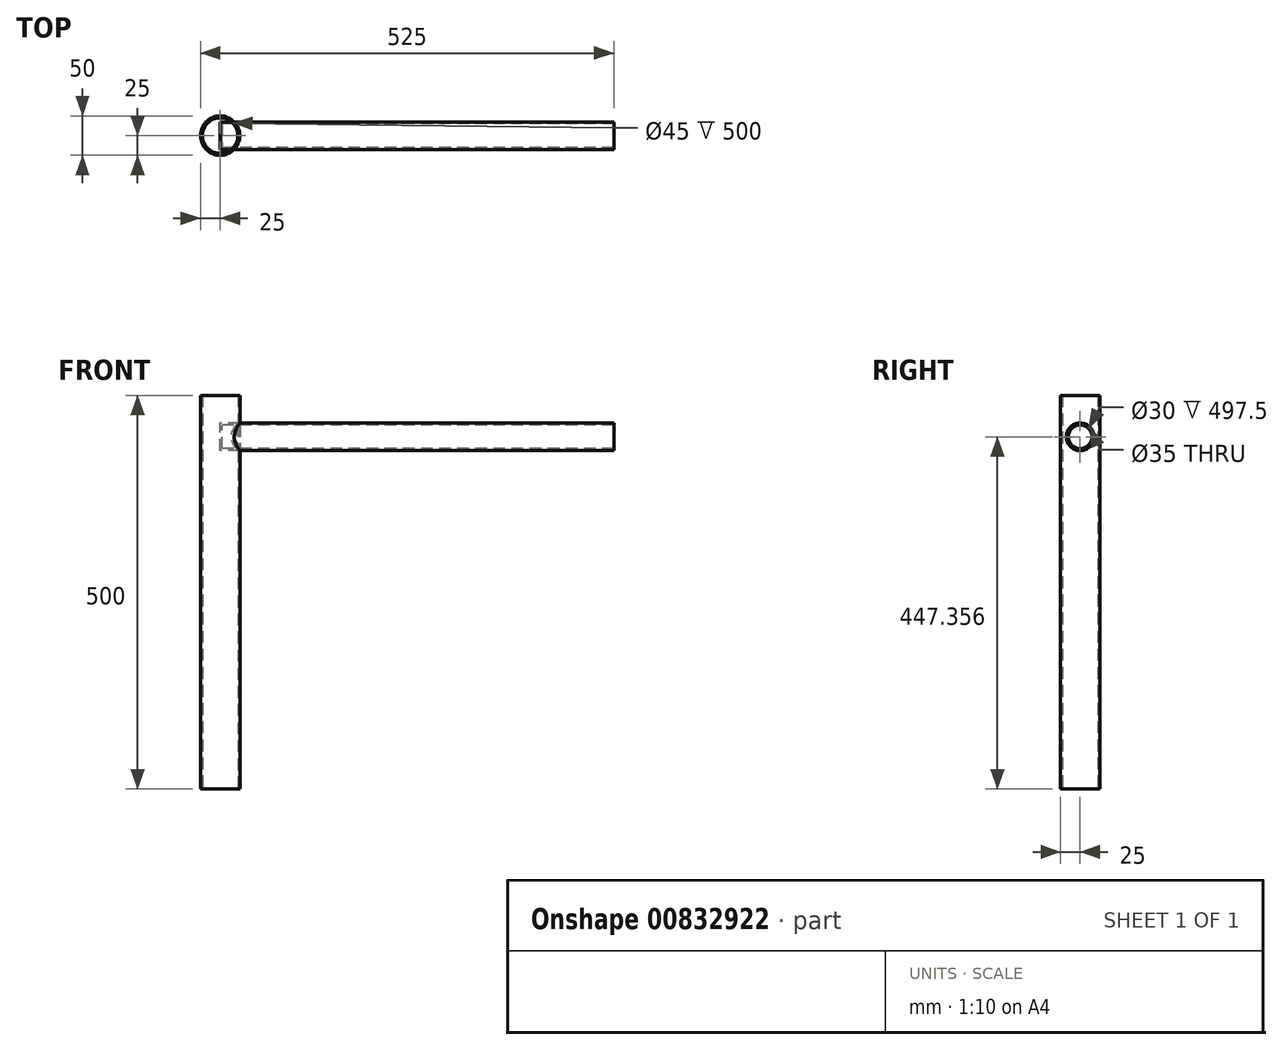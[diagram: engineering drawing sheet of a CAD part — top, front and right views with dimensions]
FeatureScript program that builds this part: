
annotation { "Feature Type Name" : "Feature", "Feature Type Description" : "" }
export const myFeature = defineFeature(function(context is Context, id is Id, definition is map)
    precondition{}
    {
        {
            var Q0;
            Q0=qCreatedBy(makeId("Top.planeOp"),FACE);
            var sketch = newSketch(context, id + "F0", { "sketchPlane" : qUnion([Q0])});
            skCircle(sketch, "E0", {"center": v(0, 0) * mm, "radius": 25 * mm});
            skSolve(sketch);
        }
        {
            var Q0;
            Q0=makeQuery(id+"F0.imprint","IMPRINT",FACE,{"disambiguationData":[TD([[makeQuery(id+"F0.imprint","IMPRINT",EDGE,{"derivedFrom":sQuery(id+"F0.wireOp",EDGE,"E0")}),1.0]])]});
            extrude(context, id + "F1", {"entities" : qUnion([Q0]), "depth" : 500 * mm, "offsetDistance" : 25 * mm});
        }
        {
            var Q0;
            Q0=qCreatedBy(makeId("Right.planeOp"),FACE);
            var sketch = newSketch(context, id + "F2", { "sketchPlane" : qUnion([Q0])});
            skCircle(sketch, "E1", {"center": v(0, 447.36) * mm, "radius": 17.5 * mm});
            skSolve(sketch);
        }
        {
            var Q0;
            Q0 = qSketchRegion(id + "F2", true);
            extrude(context, id + "F3", {"entities" : qUnion([Q0]), "depth" : 500 * mm, "offsetDistance" : 25 * mm});
        }
        {
            var Q0;
            Q0=qCreatedBy(makeId("Top.planeOp"),FACE);
            var sketch = newSketch(context, id + "F4", { "sketchPlane" : qUnion([Q0])});
            skLineSegment(sketch, "E2", {"start": v(0, 62.38) * mm, "end": v(0, -121.01) * mm});
            skSolve(sketch);
        }
        {
            var Q0;
            Q0=qCreatedBy(makeId("Top.planeOp"),FACE);
            var Q1;
            Q1=sQuery(id+"F4.wireOp",EDGE,"E2");
            cPlane(context, id + "F5", {"entities" : qUnion([Q0, Q1]), "cplaneType" : CPlaneType.LINE_ANGLE, "offset" : 25 * mm, "angle" : 45 * degree, "oppositeDirection" : true, "width" : 150 * mm, "height" : 150 * mm});
        }
        {
            var Q0;
            Q0=qCreatedBy(id+"F5.planeOp",FACE);
            var sketch = newSketch(context, id + "F6", { "sketchPlane" : qUnion([Q0])});
            skLineSegment(sketch, "E3.bottom", {"start": v(-23.2, -14.3) * mm, "end": v(7.82, -14.3) * mm});
            skLineSegment(sketch, "E3.top", {"start": v(-23.2, 14.12) * mm, "end": v(7.82, 14.12) * mm});
            skLineSegment(sketch, "E3.left", {"start": v(-23.2, -14.3) * mm, "end": v(-23.2, 14.12) * mm});
            skLineSegment(sketch, "E3.right", {"start": v(7.82, -14.3) * mm, "end": v(7.82, 14.12) * mm});
            skSolve(sketch);
        }
        {
            var Q0;
            Q0 = qSketchRegion(id + "F6", true);
            extrude(context, id + "F7", {"entities" : qUnion([Q0]), "oppositeDirection" : true, "depth" : 700 * mm, "offsetDistance" : 25 * mm});
        }
        {
            var Q0;
            Q0=makeQuery(id+"F1.opExtrude","CAP_FACE",FACE,{"disambiguationData":[OSD([sQuery(id+"F0.wireOp",EDGE,"E0")])],"isStart":true});
            var Q1;
            Q1=makeQuery(id+"F7.opExtrude","CAP_FACE",FACE,{"disambiguationData":[OSD([sQuery(id+"F6.wireOp",EDGE,"E3.bottom"),sQuery(id+"F6.wireOp",EDGE,"E3.top"),sQuery(id+"F6.wireOp",EDGE,"E3.left"),sQuery(id+"F6.wireOp",EDGE,"E3.right")])],"isStart":true});
            var Q2;
            Q2=makeQuery(id+"F3.opExtrude","CAP_FACE",FACE,{"disambiguationData":[OSD([sQuery(id+"F2.wireOp",EDGE,"E1")])],"isStart":false});
            var Q3;
            Q3=makeQuery(id+"F7.opExtrude","CAP_FACE",FACE,{"disambiguationData":[OSD([sQuery(id+"F6.wireOp",EDGE,"E3.bottom"),sQuery(id+"F6.wireOp",EDGE,"E3.top"),sQuery(id+"F6.wireOp",EDGE,"E3.left"),sQuery(id+"F6.wireOp",EDGE,"E3.right")])],"isStart":false});
            var Q4;
            Q4=makeQuery(id+"F1.opExtrude","CAP_FACE",FACE,{"disambiguationData":[OSD([sQuery(id+"F0.wireOp",EDGE,"E0")])],"isStart":false});
            shell(context, id + "F8", {"entities" : qUnion([Q0, Q1, Q2, Q3, Q4]), "thickness" : 2.5 * mm});
        }
        {
            var Q0;
            Q0=makeQuery(id+"F3.opExtrude","SWEPT_BODY",BODY,{"disambiguationData":[OSD([sQuery(id+"F2.wireOp",EDGE,"E1")])]});
            var Q1;
            Q1=makeQuery(id+"F7.opExtrude","SWEPT_BODY",BODY,{"disambiguationData":[OSD([sQuery(id+"F6.wireOp",EDGE,"E3.bottom"),sQuery(id+"F6.wireOp",EDGE,"E3.top"),sQuery(id+"F6.wireOp",EDGE,"E3.left"),sQuery(id+"F6.wireOp",EDGE,"E3.right")])]});
            booleanBodies(context, id + "F9", {"operationType" : BooleanOperationType.SUBTRACTION, "tools" : qUnion([Q0]), "targets" : qUnion([Q1]), "keepTools" : true});
        }
        {
            var Q0;
            Q0=makeQuery(id+"F9.opBoolean","SPLIT",BODY,{"disambiguationData":[OD(2.0)],"derivedFrom":makeQuery(id+"F7.opExtrude","SWEPT_BODY",BODY,{"disambiguationData":[OSD([sQuery(id+"F6.wireOp",EDGE,"E3.bottom"),sQuery(id+"F6.wireOp",EDGE,"E3.top"),sQuery(id+"F6.wireOp",EDGE,"E3.left"),sQuery(id+"F6.wireOp",EDGE,"E3.right")])]})});
            deleteBodies(context, id + "F10", {"entities" : qUnion([Q0])});
        }
        {
            var Q0;
            Q0=makeQuery(id+"F3.opExtrude","SWEPT_BODY",BODY,{"disambiguationData":[OSD([sQuery(id+"F2.wireOp",EDGE,"E1")])]});
            var Q1;
            Q1=makeQuery(id+"F1.opExtrude","SWEPT_BODY",BODY,{"disambiguationData":[OSD([sQuery(id+"F0.wireOp",EDGE,"E0")])]});
            booleanBodies(context, id + "F11", {"operationType" : BooleanOperationType.SUBTRACTION, "tools" : qUnion([Q0]), "targets" : qUnion([Q1]), "keepTools" : true});
        }
    });
